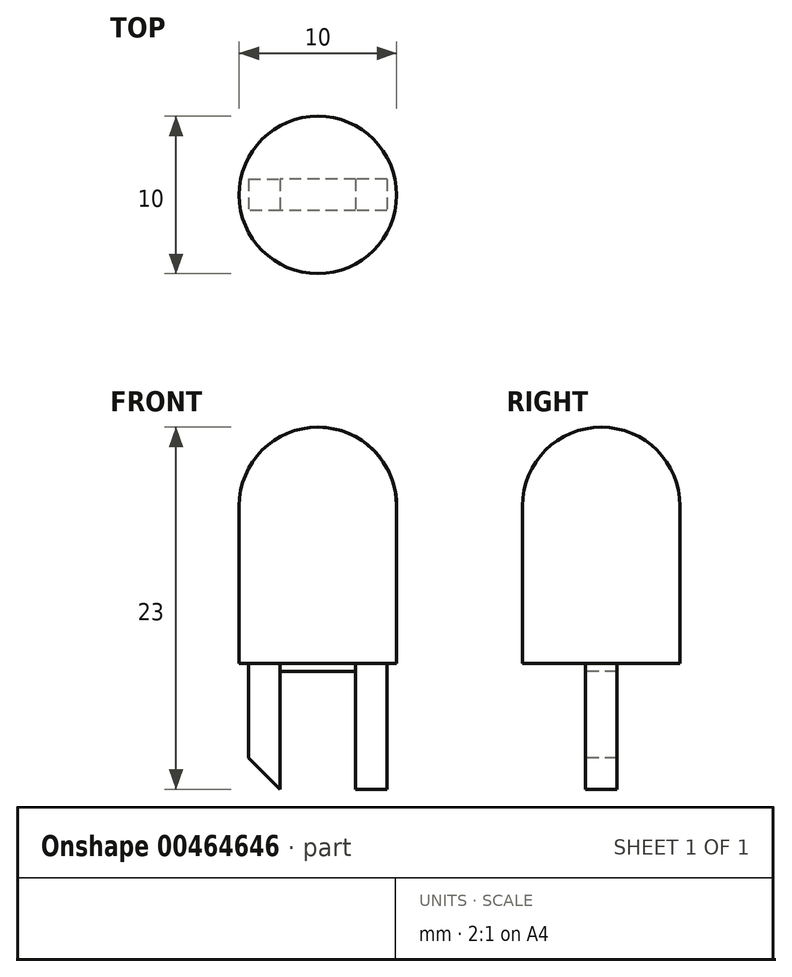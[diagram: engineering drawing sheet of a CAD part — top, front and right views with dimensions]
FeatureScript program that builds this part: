
annotation { "Feature Type Name" : "Feature", "Feature Type Description" : "" }
export const myFeature = defineFeature(function(context is Context, id is Id, definition is map)
    precondition{}
    {
        {
            assignVariable(context, id + "F0", {"name" : "body_diameter", "anyValue" : 10});
        }
        {
            assignVariable(context, id + "F1", {"name" : "body_height", "anyValue" : 15});
        }
        {
            var Q0;
            Q0=qCreatedBy(makeId("Top.planeOp"),FACE);
            var sketch = newSketch(context, id + "F2", { "sketchPlane" : qUnion([Q0])});
            skCircle(sketch, "E0", {"center": v(0, 0) * mm, "radius": 5 * mm});
            skSolve(sketch);
        }
        {
            var Q0;
            Q0=makeQuery(id+"F2.imprint","IMPRINT",FACE,{"disambiguationData":[TD([[makeQuery(id+"F2.imprint","IMPRINT",EDGE,{"derivedFrom":sQuery(id+"F2.wireOp",EDGE,"E0")}),1.0]])]});
            var Q1;
            Q1=sQuery(id+"F2.wireOp",EDGE,"E0");
            extrude(context, id + "F3", {"entities" : qUnion([Q0]), "surfaceEntities" : qUnion([Q1]), "depth" : (getVariable(context, 'body_height')) * mm});
        }
        {
            var Q0;
            Q0=makeQuery(id+"F3.opExtrude","CAP_EDGE",EDGE,{"disambiguationData":[OSD([sQuery(id+"F2.wireOp",EDGE,"E0")])],"isStart":false});
            fillet(context, id + "F4", {"entities" : qUnion([Q0]), "radius" : (getVariable(context, 'body_diameter') - 5) * mm, "tangentPropagation" : true, "rho" : 0, "crossSection" : FilletCrossSection.CONIC, "allowEdgeOverflow" : false});
        }
        {
            assignVariable(context, id + "F5", {"name" : "leg_length", "anyValue" : 8});
        }
        {
            var Q0;
            Q0=makeQuery(id+"F3.opExtrude","CAP_FACE",FACE,{"disambiguationData":[OSD([sQuery(id+"F2.wireOp",EDGE,"E0")])],"isStart":true});
            var sketch = newSketch(context, id + "F6", { "sketchPlane" : qUnion([Q0])});
            skLineSegment(sketch, "E1.bottom", {"start": v(-2.4, -1) * mm, "end": v(-4.4, -1) * mm});
            skLineSegment(sketch, "E1.top", {"start": v(-2.4, 1) * mm, "end": v(-4.4, 1) * mm});
            skLineSegment(sketch, "E1.left", {"start": v(-2.4, -1) * mm, "end": v(-2.4, 1) * mm});
            skLineSegment(sketch, "E1.right", {"start": v(-4.4, -1) * mm, "end": v(-4.4, 1) * mm});
            skPoint(sketch, "E1.middle", {"position": v(-3.4, 0) * mm});
            skLineSegment(sketch, "E2.bottom", {"start": v(4.4, -1) * mm, "end": v(2.4, -1) * mm});
            skLineSegment(sketch, "E2.top", {"start": v(4.4, 1) * mm, "end": v(2.4, 1) * mm});
            skLineSegment(sketch, "E2.left", {"start": v(4.4, -1) * mm, "end": v(4.4, 1) * mm});
            skLineSegment(sketch, "E2.right", {"start": v(2.4, -1) * mm, "end": v(2.4, 1) * mm});
            skPoint(sketch, "E2.middle", {"position": v(3.4, 0) * mm});
            skLineSegment(sketch, "E3.bottom", {"start": v(2.4, 1) * mm, "end": v(-2.4, 1) * mm});
            skLineSegment(sketch, "E3.top", {"start": v(2.4, -1) * mm, "end": v(-2.4, -1) * mm});
            skLineSegment(sketch, "E3.left", {"start": v(2.4, 1) * mm, "end": v(2.4, -1) * mm});
            skLineSegment(sketch, "E3.right", {"start": v(-2.4, 1) * mm, "end": v(-2.4, -1) * mm});
            skPoint(sketch, "E3.middle", {"position": v(0, 0) * mm});
            skSolve(sketch);
        }
        {
            var Q0;
            Q0=makeQuery(id+"F6.imprint","IMPRINT",FACE,{"disambiguationData":[TD([[makeQuery(id+"F6.imprint","IMPRINT",EDGE,{"derivedFrom":sQuery(id+"F6.wireOp",EDGE,"E1.bottom")}),-1.0]])]});
            var Q1;
            Q1=makeQuery(id+"F6.imprint","IMPRINT",FACE,{"disambiguationData":[TD([[makeQuery(id+"F6.imprint","IMPRINT",EDGE,{"derivedFrom":sQuery(id+"F6.wireOp",EDGE,"E2.bottom")}),-1.0]])]});
            extrude(context, id + "F7", {"entities" : qUnion([Q0, Q1]), "depth" : (getVariable(context, 'leg_length')) * mm});
        }
        {
            var Q0;
            Q0=makeQuery(id+"F7.opExtrude","CAP_EDGE",EDGE,{"disambiguationData":[OSD([sQuery(id+"F6.wireOp",EDGE,"E1.right")])],"isStart":false});
            chamfer(context, id + "F8", {"entities" : qUnion([Q0]), "width" : 2 * mm, "tangentPropagation" : true});
        }
        {
            var Q0;
            Q0=makeQuery(id+"F6.imprint","IMPRINT",FACE,{"disambiguationData":[TD([[makeQuery(id+"F6.imprint","IMPRINT",EDGE,{"derivedFrom":sQuery(id+"F6.wireOp",EDGE,"E3.bottom")}),1.0]])]});
            extrude(context, id + "F9", {"entities" : qUnion([Q0]), "depth" : .5 * mm});
        }
        {
            var Q0;
            Q0=makeQuery(id+"F3.opExtrude","SWEPT_BODY",BODY,{"disambiguationData":[OSD([sQuery(id+"F2.wireOp",EDGE,"E0")])]});
            transform(context, id + "F10", {"entities" : qUnion([Q0]), "transformType" : TransformType.TRANSLATION_3D, "dx" : 0 * mm, "dy" : 0 * mm, "dz" : 0 * mm, "makeCopy" : true});
        }
    });
